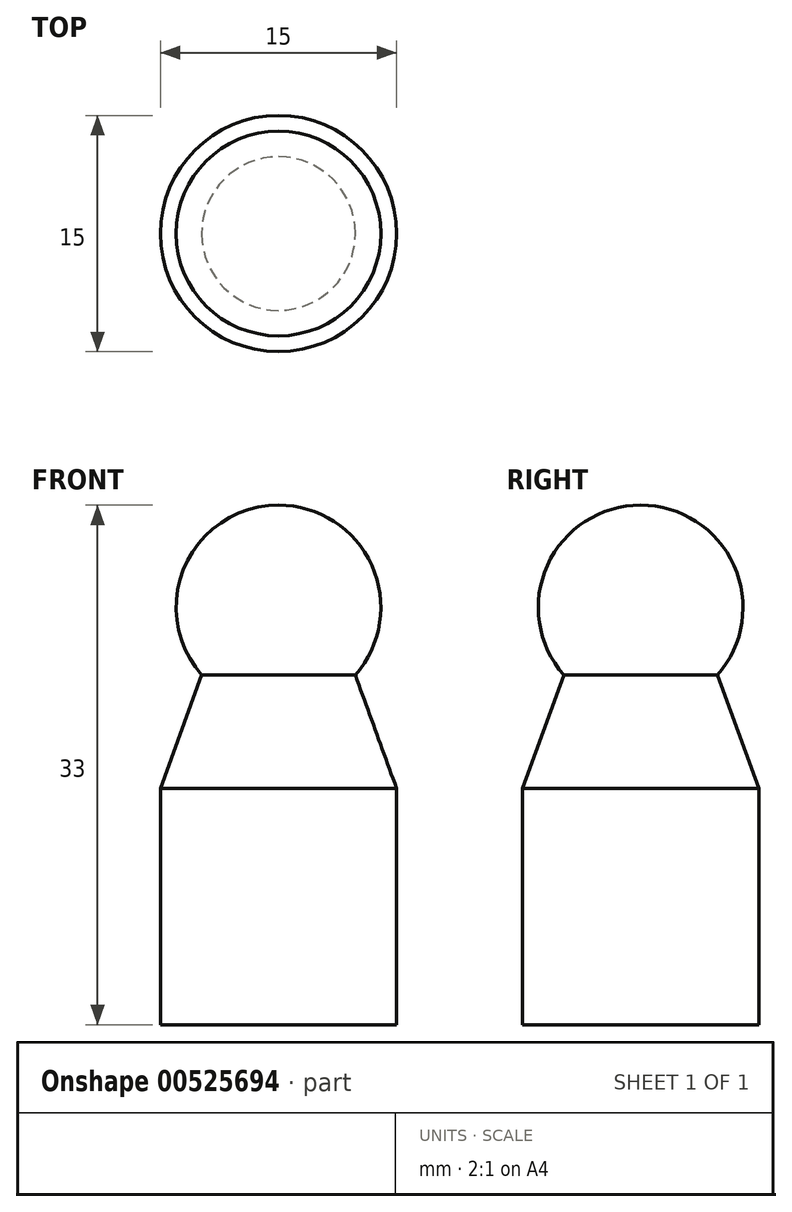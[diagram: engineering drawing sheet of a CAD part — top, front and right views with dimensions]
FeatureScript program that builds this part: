
annotation { "Feature Type Name" : "Feature", "Feature Type Description" : "" }
export const myFeature = defineFeature(function(context is Context, id is Id, definition is map)
    precondition{}
    {
        {
            var Q0;
            Q0=qCreatedBy(makeId("Top.planeOp"),FACE);
            var sketch = newSketch(context, id + "F0", { "sketchPlane" : qUnion([Q0])});
            skCircle(sketch, "E0", {"center": v(0, 0) * mm, "radius": 7.5 * mm});
            skSolve(sketch);
        }
        {
            var Q0;
            Q0 = qSketchRegion(id + "F0", true);
            extrude(context, id + "F1", {"entities" : qUnion([Q0]), "depth" : 15 * mm, "offsetDistance" : 25 * mm});
        }
        {
            var Q0;
            Q0=makeQuery(id+"F1.opExtrude","CAP_FACE",FACE,{"disambiguationData":[OSD([sQuery(id+"F0.wireOp",EDGE,"E0")])],"isStart":false});
            extrude(context, id + "F2", {"entities" : qUnion([Q0]), "operationType" : NewBodyOperationType.ADD, "depth" : 10 * mm, "offsetDistance" : 25 * mm, "hasDraft" : true, "draftAngle" : 20 * degree, "draftPullDirection" : true});
        }
        {
            var Q0;
            Q0=qCreatedBy(makeId("Front.planeOp"),FACE);
            var sketch = newSketch(context, id + "F3", { "sketchPlane" : qUnion([Q0])});
            skArc(sketch, "E1", {"start": v(0, 20) * mm, "mid": v(6.5, 26.5) * mm, "end": v(0, 33) * mm});
            skLineSegment(sketch, "E2.0", {"start": v(-7.5, 15) * mm, "end": v(7.5, 15) * mm, "construction": true});
            skLineSegment(sketch, "E3", {"start": v(0, 20) * mm, "end": v(0, 33) * mm});
            skSolve(sketch);
        }
        {
            var Q0;
            Q0 = qSketchRegion(id + "F3", true);
            var Q1;
            Q1=sQuery(id+"F3.wireOp",EDGE,"E3");
            revolve(context, id + "F4", {"operationType" : NewBodyOperationType.ADD, "entities" : qUnion([Q0]), "axis" : qUnion([Q1]), "revolveType" : RevolveType.FULL});
        }
    });
